annotation { "Feature Type Name" : "Feature", "Feature Type Description" : "" }
export const myFeature = defineFeature(function(context is Context, id is Id, definition is map)
    precondition{}
    {
        {
            var Q0;
            Q0=qCreatedBy(makeId("Top.planeOp"),FACE);
            var sketch = newSketch(context, id + "F0", { "sketchPlane" : qUnion([Q0])});
            skLineSegment(sketch, "E0.bottom", {"start": v(-35.5, 62.87) * mm, "end": v(35.5, 62.87) * mm});
            skLineSegment(sketch, "E0.top", {"start": v(-35.5, -62.87) * mm, "end": v(35.5, -62.87) * mm});
            skLineSegment(sketch, "E0.left", {"start": v(-41.85, 56.51) * mm, "end": v(-41.85, -56.52) * mm});
            skLineSegment(sketch, "E0.right", {"start": v(41.85, 56.52) * mm, "end": v(41.85, -56.51) * mm});
            skPoint(sketch, "E1.visualSharp", {"position": v(-41.85, 62.86) * mm});
            skArc(sketch, "E1.filletArc", {"start": v(-35.5, 62.87) * mm, "mid": v(-39.99, 61) * mm, "end": v(-41.85, 56.51) * mm});
            skPoint(sketch, "E2.visualSharp", {"position": v(41.85, 62.87) * mm});
            skArc(sketch, "E2.filletArc", {"start": v(41.85, 56.52) * mm, "mid": v(39.99, 61) * mm, "end": v(35.5, 62.87) * mm});
            skPoint(sketch, "E3.visualSharp", {"position": v(-41.85, -62.87) * mm});
            skArc(sketch, "E3.filletArc", {"start": v(-41.85, -56.52) * mm, "mid": v(-39.99, -61) * mm, "end": v(-35.5, -62.87) * mm});
            skPoint(sketch, "E4.visualSharp", {"position": v(41.85, -62.87) * mm});
            skArc(sketch, "E4.filletArc", {"start": v(35.5, -62.87) * mm, "mid": v(39.99, -61) * mm, "end": v(41.85, -56.51) * mm});
            skSolve(sketch);
        }
        {
            var Q0;
            Q0 = qSketchRegion(id + "F0", true);
            extrude(context, id + "F1", {"entities" : qUnion([Q0]), "depth" : 11.7 * mm});
        }
        {
            var Q0;
            Q0=makeQuery(id+"F1.opExtrude","CAP_FACE",FACE,{"disambiguationData":[OSD([sQuery(id+"F0.wireOp",EDGE,"E0.bottom"),sQuery(id+"F0.wireOp",EDGE,"E0.top"),sQuery(id+"F0.wireOp",EDGE,"E0.left"),sQuery(id+"F0.wireOp",EDGE,"E0.right")])],"isStart":false});
            var sketch = newSketch(context, id + "F2", { "sketchPlane" : qUnion([Q0])});
            skLineSegment(sketch, "E5.bottom", {"start": v(-34.42, 52.2) * mm, "end": v(34.42, 52.2) * mm});
            skLineSegment(sketch, "E5.top", {"start": v(-34.42, -52.2) * mm, "end": v(34.42, -52.2) * mm});
            skLineSegment(sketch, "E5.left", {"start": v(-34.42, 52.2) * mm, "end": v(-34.42, -52.2) * mm});
            skLineSegment(sketch, "E5.right", {"start": v(34.42, 52.2) * mm, "end": v(34.42, -52.2) * mm});
            skSolve(sketch);
        }
        {
            var Q0;
            Q0 = qSketchRegion(id + "F2", true);
            var Q1;
            Q1 = qSketchRegion(id + "F4", true);
            extrude(context, id + "F3", {"entities" : qUnion([Q0, Q1]), "operationType" : NewBodyOperationType.REMOVE, "oppositeDirection" : true, "depth" : 18.54 * mm});
        }
        {
            var Q0;
            Q0=makeQuery(id+"F1.opExtrude","CAP_FACE",FACE,{"disambiguationData":[OSD([sQuery(id+"F0.wireOp",EDGE,"E0.bottom"),sQuery(id+"F0.wireOp",EDGE,"E0.top"),sQuery(id+"F0.wireOp",EDGE,"E0.left"),sQuery(id+"F0.wireOp",EDGE,"E0.right")])],"isStart":false});
            var sketch = newSketch(context, id + "F4", { "sketchPlane" : qUnion([Q0])});
            skLineSegment(sketch, "E6.bottom", {"start": v(-37.05, 55.12) * mm, "end": v(37.02, 55.12) * mm});
            skLineSegment(sketch, "E6.top", {"start": v(-37.05, -55.12) * mm, "end": v(37.02, -55.12) * mm});
            skLineSegment(sketch, "E6.left", {"start": v(-37.05, 55.12) * mm, "end": v(-37.05, -55.12) * mm});
            skLineSegment(sketch, "E6.right", {"start": v(37.02, 55.12) * mm, "end": v(37.02, -55.12) * mm});
            skLineSegment(sketch, "E7.bottom", {"start": v(-34.52, 62.03) * mm, "end": v(34.52, 62.03) * mm});
            skLineSegment(sketch, "E7.top", {"start": v(-33.86, -62.03) * mm, "end": v(33.86, -62.03) * mm});
            skLineSegment(sketch, "E7.left", {"start": v(-40.87, 55.68) * mm, "end": v(-40.87, -55.02) * mm});
            skLineSegment(sketch, "E7.right", {"start": v(40.87, 55.68) * mm, "end": v(40.87, -55.02) * mm});
            skPoint(sketch, "E8.visualSharp", {"position": v(-40.87, 62.03) * mm});
            skArc(sketch, "E8.filletArc", {"start": v(-34.52, 62.03) * mm, "mid": v(-39.02, 60.17) * mm, "end": v(-40.87, 55.68) * mm});
            skPoint(sketch, "E9.visualSharp", {"position": v(40.87, 62.03) * mm});
            skArc(sketch, "E9.filletArc", {"start": v(40.87, 55.68) * mm, "mid": v(39.02, 60.17) * mm, "end": v(34.52, 62.03) * mm});
            skLineSegment(sketch, "E10", {"start": v(-40.87, -55.02) * mm, "end": v(-33.86, -62.03) * mm});
            skLineSegment(sketch, "E11", {"start": v(33.86, -62.03) * mm, "end": v(40.87, -55.02) * mm});
            skPoint(sketch, "E12.orphan", {"position": v(-40.87, -62.03) * mm});
            skPoint(sketch, "E13.orphan", {"position": v(40.87, -62.03) * mm});
            skLineSegment(sketch, "E14", {"start": v(-37.05, -55.12) * mm, "end": v(-34.42, -52.2) * mm, "construction": true});
            skPoint(sketch, "E15.orphan", {"position": v(34.42, -52.2) * mm});
            skLineSegment(sketch, "E16", {"start": v(37.02, 55.12) * mm, "end": v(37.02, 55.12) * mm});
            skLineSegment(sketch, "E17", {"start": v(-37.05, 55.12) * mm, "end": v(-37.05, 55.12) * mm});
            skLineSegment(sketch, "E18", {"start": v(-37.05, -55.12) * mm, "end": v(-37.05, -55.12) * mm});
            skLineSegment(sketch, "E19", {"start": v(37.02, -55.12) * mm, "end": v(37.02, -55.12) * mm});
            skLineSegment(sketch, "E20", {"start": v(-37.05, 55.12) * mm, "end": v(-34.42, 52.2) * mm, "construction": true});
            skLineSegment(sketch, "E21", {"start": v(37.02, 55.12) * mm, "end": v(34.42, 52.2) * mm, "construction": true});
            skLineSegment(sketch, "E22", {"start": v(34.42, -52.2) * mm, "end": v(37.02, -55.12) * mm, "construction": true});
            skSolve(sketch);
        }
        {
            var Q0;
            Q0=makeQuery(id+"F4.imprint","IMPRINT",FACE,{"disambiguationData":[TD([[makeQuery(id+"F4.imprint","IMPRINT",EDGE,{"derivedFrom":sQuery(id+"F4.wireOp",EDGE,"E7.bottom")}),1.0]])]});
            var Q1;
            Q1=makeQuery(id+"F4.imprint","IMPRINT",FACE,{"disambiguationData":[TD([[makeQuery(id+"F4.imprint","IMPRINT",EDGE,{"derivedFrom":makeQuery(id+"F3.boolean.opBoolean","COPY",EDGE,{"derivedFrom":makeQuery(id+"F3.opExtrude","CAP_EDGE",EDGE,{"disambiguationData":[OSD([sQuery(id+"F2.wireOp",EDGE,"E5.bottom")])],"isStart":true})})}),1.0]])]});
            extrude(context, id + "F5", {"entities" : qUnion([Q0, Q1]), "operationType" : NewBodyOperationType.REMOVE, "oppositeDirection" : true, "depth" : 10.23 * mm});
        }
        {
            var Q0;
            Q0=makeQuery(id+"F1.opExtrude","CAP_FACE",FACE,{"disambiguationData":[OSD([sQuery(id+"F0.wireOp",EDGE,"E0.bottom"),sQuery(id+"F0.wireOp",EDGE,"E0.top"),sQuery(id+"F0.wireOp",EDGE,"E0.left"),sQuery(id+"F0.wireOp",EDGE,"E0.right"),sQuery(id+"F0.wireOp",EDGE,"E1.filletArc"),sQuery(id+"F0.wireOp",EDGE,"E2.filletArc"),sQuery(id+"F0.wireOp",EDGE,"E3.filletArc"),sQuery(id+"F0.wireOp",EDGE,"E4.filletArc")])],"isStart":false});
            var sketch = newSketch(context, id + "F6", { "sketchPlane" : qUnion([Q0])});
            skText(sketch, "E23", { "text": "H G F E D C B A", "fontName": "OpenSans-Regular.ttf"});
            skText(sketch, "E24", { "text": "CEM MGH", "fontName": "OpenSans-Bold.ttf"});
            const initialGuessF6  = {"E23": [-0.03427, 0.05466, 1, 0, 0.007], "E24": [-0.01909, -0.06083, 1, 0, 0.00572]};
            skSetInitialGuess(sketch, initialGuessF6);
            skSolve(sketch);
        }
        {
            var Q0;
            Q0 = qSketchRegion(id + "F6", true);
            extrude(context, id + "F7", {"entities" : qUnion([Q0]), "operationType" : NewBodyOperationType.REMOVE, "oppositeDirection" : true, "depth" : 1.5 * mm});
        }
    });